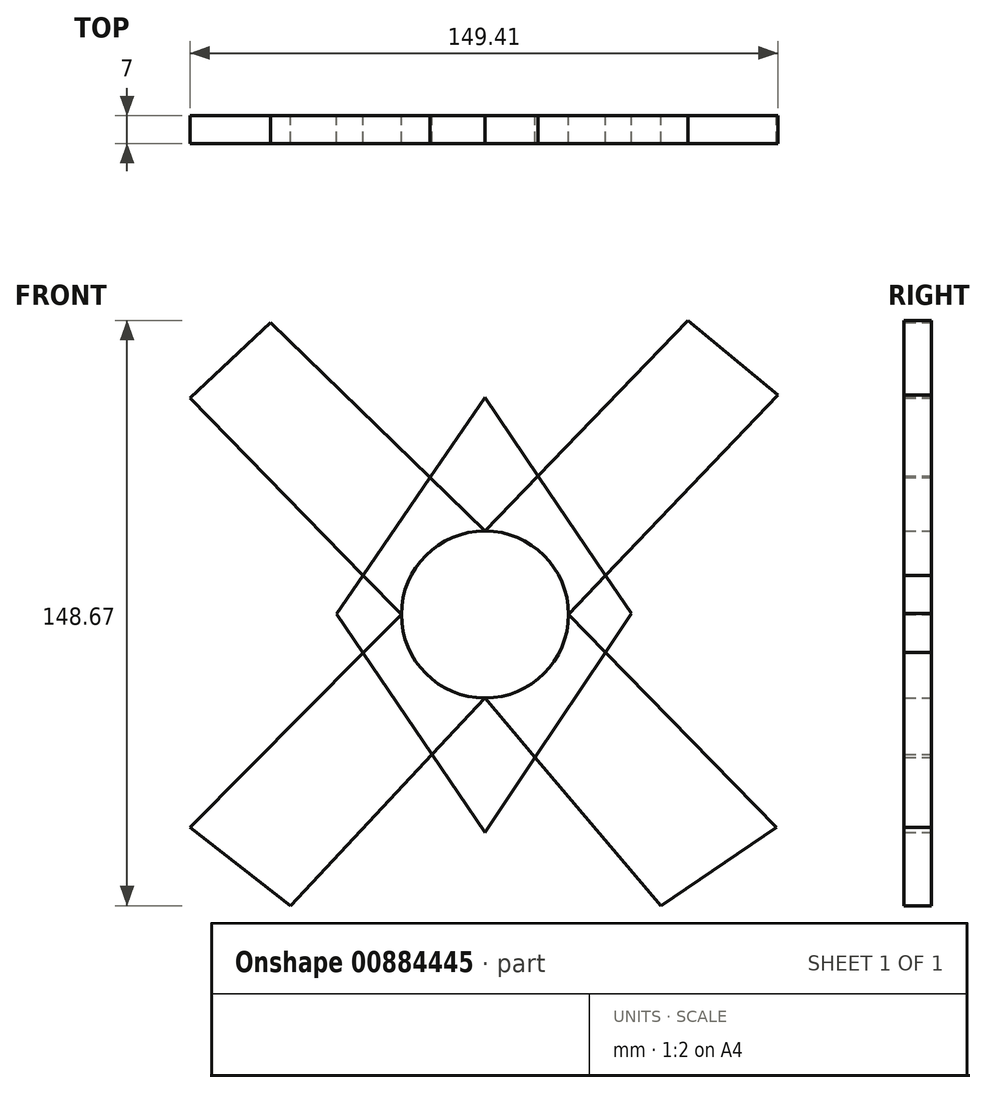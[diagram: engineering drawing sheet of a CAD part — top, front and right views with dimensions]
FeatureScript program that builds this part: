
annotation { "Feature Type Name" : "Feature", "Feature Type Description" : "" }
export const myFeature = defineFeature(function(context is Context, id is Id, definition is map)
    precondition{}
    {
        {
            var Q0;
            Q0=qCreatedBy(makeId("Front.planeOp"),FACE);
            var sketch = newSketch(context, id + "F0", { "sketchPlane" : qUnion([Q0])});
            skCircle(sketch, "E0", {"center": v(0, 0) * mm, "radius": 21.22 * mm});
            skLineSegment(sketch, "E1", {"start": v(21.22, 0) * mm, "end": v(74.07, -54.1) * mm});
            skLineSegment(sketch, "E2", {"start": v(74.07, -54.1) * mm, "end": v(44.77, -73.97) * mm});
            skLineSegment(sketch, "E3", {"start": v(44.77, -73.97) * mm, "end": v(0, -21.22) * mm});
            skLineSegment(sketch, "E4", {"start": v(0, -21.22) * mm, "end": v(-49.43, -73.97) * mm});
            skLineSegment(sketch, "E5", {"start": v(-49.43, -73.97) * mm, "end": v(-74.95, -54.1) * mm});
            skLineSegment(sketch, "E6", {"start": v(-74.95, -54.1) * mm, "end": v(-21.22, 0) * mm});
            skLineSegment(sketch, "E7", {"start": v(-21.22, 0) * mm, "end": v(-74.95, 55) * mm});
            skLineSegment(sketch, "E8", {"start": v(-74.95, 55) * mm, "end": v(-54.42, 74.21) * mm});
            skLineSegment(sketch, "E9", {"start": v(-54.42, 74.21) * mm, "end": v(0, 21.22) * mm});
            skPoint(sketch, "E10.end.orphan", {"position": v(74.07, 49.46) * mm});
            skPoint(sketch, "E11.end.orphan", {"position": v(44.77, 74.21) * mm});
            skLineSegment(sketch, "E12", {"start": v(74.46, 55.81) * mm, "end": v(21.22, 0) * mm});
            skPoint(sketch, "E13.end.orphan", {"position": v(49.19, 74.21) * mm});
            skLineSegment(sketch, "E14", {"start": v(74.46, 55.81) * mm, "end": v(51.64, 74.7) * mm});
            skLineSegment(sketch, "E15", {"start": v(51.64, 74.7) * mm, "end": v(0, 21.22) * mm});
            skLineSegment(sketch, "E16", {"start": v(0, 55.08) * mm, "end": v(-74.95, -54.1) * mm});
            skLineSegment(sketch, "E17", {"start": v(74.07, -54.1) * mm, "end": v(0, 55.08) * mm});
            skLineSegment(sketch, "E18", {"start": v(-74.95, 55) * mm, "end": v(0, -55.32) * mm});
            skLineSegment(sketch, "E19", {"start": v(0, -55.32) * mm, "end": v(74.46, 55.81) * mm});
            skSolve(sketch);
        }
        {
            var Q0;
            {var subQ0=sQuery(id+"F0.wireOp",EDGE,"E0");var subQ1=makeQuery(id+"F0.imprint","INTERSECT",VERTEX,{"derivedFrom":[subQ0,sQuery(id+"F0.wireOp",EDGE,"E1"),sQuery(id+"F0.wireOp",EDGE,"E12")]});Q0=makeQuery(id+"F0.imprint","IMPRINT",FACE,{"disambiguationData":[TD([[makeQuery(id+"F0.imprint","IMPRINT",EDGE,{"disambiguationData":[TD([[subQ1,-1.0]])],"derivedFrom":subQ0}),1.0]])]});}
            var Q1;
            {var subQ3=sQuery(id+"F0.wireOp",EDGE,"E16");var subQ5=sQuery(id+"F0.wireOp",EDGE,"E17");var subQ7=makeQuery(id+"F0.imprint","INTERSECT",VERTEX,{"derivedFrom":[subQ3,subQ5]});Q1=makeQuery(id+"F0.imprint","IMPRINT",FACE,{"disambiguationData":[TD([[makeQuery(id+"F0.imprint","IMPRINT",EDGE,{"disambiguationData":[TD([[subQ7,-1.0]])],"derivedFrom":subQ3}),1.0]])]});}
            var Q2;
            {var subQ3=sQuery(id+"F0.wireOp",EDGE,"E19");var subQ5=sQuery(id+"F0.wireOp",EDGE,"E18");var subQ7=makeQuery(id+"F0.imprint","INTERSECT",VERTEX,{"derivedFrom":[subQ5,subQ3]});Q2=makeQuery(id+"F0.imprint","IMPRINT",FACE,{"disambiguationData":[TD([[makeQuery(id+"F0.imprint","IMPRINT",EDGE,{"disambiguationData":[TD([[subQ7,1.0]])],"derivedFrom":subQ5}),1.0]])]});}
            var Q3;
            {var subQ3=sQuery(id+"F0.wireOp",EDGE,"E19");var subQ5=sQuery(id+"F0.wireOp",EDGE,"E17");var subQ6=makeQuery(id+"F0.imprint","INTERSECT",VERTEX,{"derivedFrom":[subQ5,subQ3]});Q3=makeQuery(id+"F0.imprint","IMPRINT",FACE,{"disambiguationData":[TD([[makeQuery(id+"F0.imprint","IMPRINT",EDGE,{"disambiguationData":[TD([[subQ6,-1.0]])],"derivedFrom":subQ5}),1.0]])]});}
            var Q4;
            {var subQ3=sQuery(id+"F0.wireOp",EDGE,"E18");var subQ5=sQuery(id+"F0.wireOp",EDGE,"E16");var subQ6=makeQuery(id+"F0.imprint","INTERSECT",VERTEX,{"derivedFrom":[subQ5,subQ3]});Q4=makeQuery(id+"F0.imprint","IMPRINT",FACE,{"disambiguationData":[TD([[makeQuery(id+"F0.imprint","IMPRINT",EDGE,{"disambiguationData":[TD([[subQ6,1.0]])],"derivedFrom":subQ5}),1.0]])]});}
            var Q5;
            {var subQ0=sQuery(id+"F0.wireOp",EDGE,"E14");Q5=makeQuery(id+"F0.imprint","IMPRINT",FACE,{"disambiguationData":[TD([[makeQuery(id+"F0.imprint","IMPRINT",EDGE,{"derivedFrom":subQ0}),1.0]])]});}
            var Q6;
            {var subQ0=sQuery(id+"F0.wireOp",EDGE,"E8");Q6=makeQuery(id+"F0.imprint","IMPRINT",FACE,{"disambiguationData":[TD([[makeQuery(id+"F0.imprint","IMPRINT",EDGE,{"derivedFrom":subQ0}),-1.0]])]});}
            var Q7;
            {var subQ0=sQuery(id+"F0.wireOp",EDGE,"E5");Q7=makeQuery(id+"F0.imprint","IMPRINT",FACE,{"disambiguationData":[TD([[makeQuery(id+"F0.imprint","IMPRINT",EDGE,{"derivedFrom":subQ0}),-1.0]])]});}
            var Q8;
            {var subQ0=sQuery(id+"F0.wireOp",EDGE,"E2");Q8=makeQuery(id+"F0.imprint","IMPRINT",FACE,{"disambiguationData":[TD([[makeQuery(id+"F0.imprint","IMPRINT",EDGE,{"derivedFrom":subQ0}),-1.0]])]});}
            extrude(context, id + "F1", {"entities" : qUnion([Q0, Q1, Q2, Q3, Q4, Q5, Q6, Q7, Q8]), "depth" : 7 * mm, "offsetDistance" : 25 * mm});
        }
    });
